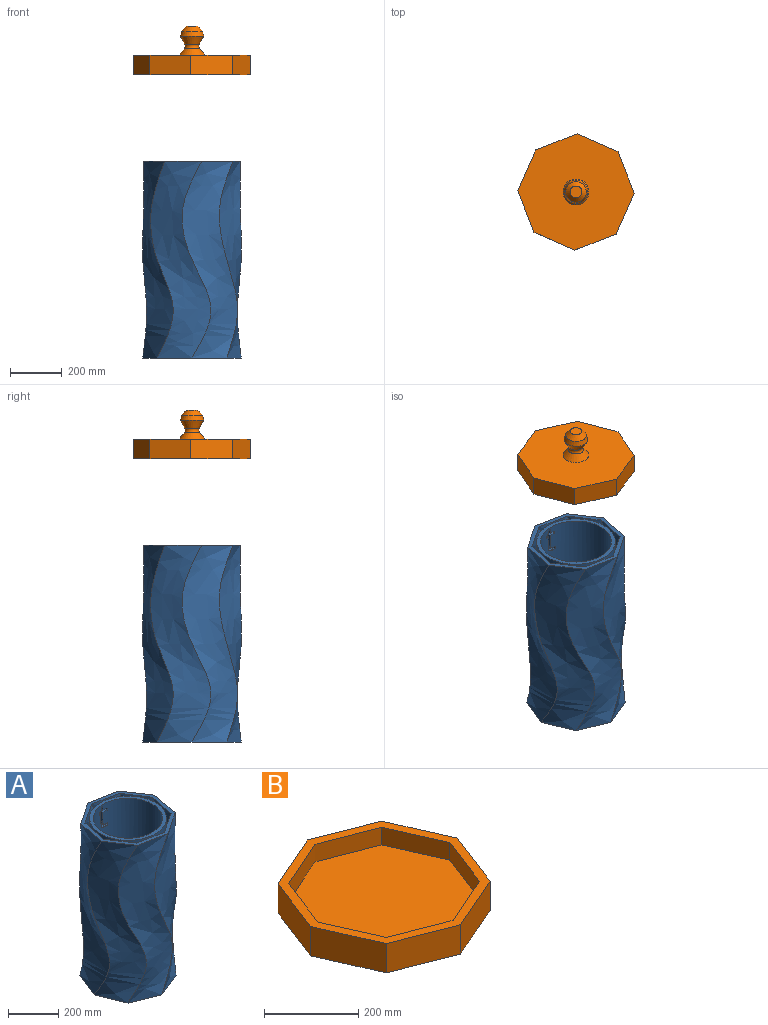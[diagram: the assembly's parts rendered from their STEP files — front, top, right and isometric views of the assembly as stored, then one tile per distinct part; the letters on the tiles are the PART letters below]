
ASSEMBLY  parts=2 mates=2
PART A: 212 faces, bbox 425.9x425.9x799.9 mm
  f0: plane 343.68x343.68mm, normal (0,0,1), area 70478.9mm2, adj f1,f3,f4,f6,f17,f18,f19,f20
  f1: cylinder r=137.18mm len=746.76mm, axis (0,0,-1), area 625380mm2, adj f0,f2,f27,f28,f29,f30,f31,f32
  f2: cylinder r=137.18mm len=34.63mm, axis (0,0,-1), area 741.5mm2, adj f1,f93,f94,f95,f96,f97,f98,f99
  f3: cylinder r=137.18mm len=48.52mm, axis (0,0,-1), area 1293.6mm2, adj f0,f128,f129,f130,f131,f132,f135
  f4: cylinder r=152.42mm len=746.76mm, axis (0,0,-1), area 696902.1mm2, adj f0,f5,f27,f28,f29,f30,f31,f32
  f5: cylinder r=152.42mm len=34.63mm, axis (0,0,-1), area 741mm2, adj f4,f93,f94,f95,f96,f97,f98,f99
  f6: cylinder r=152.42mm len=48.52mm, axis (0,0,-1), area 1293.2mm2, adj f0,f128,f129,f130,f131,f132,f135
  f7: plane 373.92x373.92mm, normal (0,0,1), area 17183mm2, adj f9,f10,f11,f12,f13,f14,f15,f16
  f8: plane 381x381mm, normal (0,0,-1), area 102644.3mm2, adj f9,f10,f11,f12,f13,f14,f15,f16
  f9: bspline ~769.42x258.19mm, area 110884.9mm2, adj f7,f8,f10,f16
  f10: bspline ~769.42x285.68mm, area 110884.9mm2, adj f7,f8,f9,f11
  f11: bspline ~769.42x258.19mm, area 110884.9mm2, adj f7,f8,f10,f12
  f12: bspline ~769.42x285.68mm, area 110884.9mm2, adj f7,f8,f11,f13
  f13: bspline ~769.42x258.19mm, area 110884.9mm2, adj f7,f8,f12,f14
  f14: bspline ~769.42x285.68mm, area 110884.9mm2, adj f7,f8,f13,f15
  f15: bspline ~769.42x258.19mm, area 110884.9mm2, adj f7,f8,f14,f16
  f16: bspline ~769.42x285.68mm, area 110884.9mm2, adj f7,f8,f9,f15
  f17: offset ~799.9x288.67mm, area 99034mm2, adj f0,f7,f18,f24
  f18: offset ~799.9x316.15mm, area 99034mm2, adj f0,f7,f17,f19
  f19: offset ~799.9x288.67mm, area 99034mm2, adj f0,f7,f18,f20
  f20: offset ~799.9x316.15mm, area 99034mm2, adj f0,f7,f19,f21
  f21: offset ~799.9x288.67mm, area 99034mm2, adj f0,f7,f20,f22
  f22: offset ~799.9x316.15mm, area 99034mm2, adj f0,f7,f21,f23
  f23: offset ~799.9x288.67mm, area 99034mm2, adj f0,f7,f22,f24
  f24: offset ~799.9x316.15mm, area 99034mm2, adj f0,f7,f17,f23
  f25: cylinder r=137.18mm len=48.52mm, axis (0,0,-1), area 1293.6mm2, adj f0,f104,f105,f106,f107,f108,f109
  f26: cylinder r=152.42mm len=48.52mm, axis (0,0,-1), area 1293.2mm2, adj f0,f104,f105,f106,f107,f108,f109
  f27: plane 304.84x304.84mm, normal (0,0,1), area 13865.6mm2, adj f1,f4
  f28: plane 15.64x9.99mm, normal (-0.99,0,0.15), area 155.6mm2, adj f1,f4,f29,f40
  f29: extruded ~16.26x7.78mm, area 120.7mm2, adj f1,f4,f28,f30
  f30: extruded ~15.84x14.76mm, area 257.8mm2, adj f1,f4,f29,f31
  f31: extruded ~17.45x15.46mm, area 288.5mm2, adj f1,f4,f30,f32
  f32: plane 38.15x15.26mm, normal (-1,0,0), area 582.3mm2, adj f1,f4,f31,f33
  f33: plane 16.32x10.77mm, normal (0,0,1), area 164.9mm2, adj f1,f4,f32,f34
  f34: plane 71.09x15.37mm, normal (1,0,0), area 1092.6mm2, adj f1,f4,f33,f35
  f35: plane 16.21x8.88mm, normal (0,0,-1), area 136.1mm2, adj f1,f4,f34,f36
  f36: plane 15.35x13.16mm, normal (-1,0,-0.09), area 201.9mm2, adj f1,f4,f35,f37
  f37: plane 15.3x0.52mm, normal (0,0,-1), area 7.9mm2, adj f1,f4,f36,f38
  f38: extruded ~15.47x10.7mm, area 220.5mm2, adj f1,f4,f37,f39
  f39: extruded ~15.92x12.27mm, area 199mm2, adj f1,f4,f38,f40
  f40: extruded ~16.43x8.49mm, area 131.2mm2, adj f1,f4,f28,f39
  f41: extruded ~16.43x8.49mm, area 131.2mm2, adj f1,f4,f42,f53
  f42: extruded ~15.92x12.27mm, area 199mm2, adj f1,f4,f41,f43
  f43: extruded ~15.47x10.7mm, area 220.5mm2, adj f1,f4,f42,f44
  f44: plane 15.3x0.52mm, normal (0,0,-1), area 7.9mm2, adj f1,f4,f43,f45
  f45: plane 15.35x13.16mm, normal (-1,0,-0.09), area 201.9mm2, adj f1,f4,f44,f46
  f46: plane 16.21x8.88mm, normal (0,0,-1), area 136.1mm2, adj f1,f4,f45,f47
  f47: plane 71.09x15.37mm, normal (1,0,0), area 1092.6mm2, adj f1,f4,f46,f48
  f48: plane 16.32x10.77mm, normal (0,0,1), area 164.9mm2, adj f1,f4,f47,f49
  f49: plane 38.15x15.26mm, normal (-1,0,0), area 582.3mm2, adj f1,f4,f48,f50
  f50: extruded ~17.45x15.46mm, area 288.5mm2, adj f1,f4,f49,f51
  f51: extruded ~15.84x14.76mm, area 257.8mm2, adj f1,f4,f50,f52
  f52: extruded ~16.26x7.78mm, area 120.7mm2, adj f1,f4,f51,f53
  f53: plane 15.64x9.99mm, normal (-0.99,0,0.15), area 155.6mm2, adj f1,f4,f41,f52
  f54: extruded ~19.21x16.14mm, area 308.3mm2, adj f1,f4,f55,f78
  f55: extruded ~20.4x17.26mm, area 322.7mm2, adj f1,f4,f54,f56
  f56: plane 15.45x9.24mm, normal (1,0,0), area 142.7mm2, adj f1,f4,f55,f57
  f57: extruded ~16.69x10.17mm, area 167.1mm2, adj f1,f4,f56,f58
  f58: extruded ~15.87x10.48mm, area 161.8mm2, adj f1,f4,f57,f59
  f59: extruded ~15.51x11.99mm, area 189mm2, adj f1,f4,f58,f60
  f60: extruded ~15.61x7.6mm, area 139.5mm2, adj f1,f4,f59,f61
  f61: extruded ~15.56x6.57mm, area 116.6mm2, adj f1,f4,f60,f62
  f62: extruded ~15.57x13mm, area 222.2mm2, adj f1,f4,f61,f63
  f63: extruded ~16.16x13.05mm, area 219.8mm2, adj f1,f4,f62,f64
  f64: extruded ~16.14x5.79mm, area 126.7mm2, adj f1,f4,f63,f65
  f65: extruded ~15.74x7.73mm, area 124.3mm2, adj f1,f4,f64,f66
  f66: extruded ~16.34x12.71mm, area 229.5mm2, adj f1,f4,f65,f67
  f67: extruded ~17.94x16.33mm, area 287.9mm2, adj f1,f4,f66,f68
  f68: extruded ~20.78x16.93mm, area 327.5mm2, adj f1,f4,f67,f69
  f69: plane 15.88x8.11mm, normal (-0.92,0,0.4), area 136.1mm2, adj f1,f4,f68,f70
  f70: extruded ~17.94x16.41mm, area 283.2mm2, adj f1,f4,f69,f71
  f71: extruded ~15.66x10.69mm, area 168.6mm2, adj f1,f4,f70,f72
  f72: extruded ~15.61x6.12mm, area 114mm2, adj f1,f4,f71,f73
  f73: extruded ~15.44x4.5mm, area 73.2mm2, adj f1,f4,f72,f74
  f74: extruded ~15.61x4.35mm, area 86.3mm2, adj f1,f4,f73,f75
  f75: extruded ~15.48x11.52mm, area 191mm2, adj f1,f4,f74,f76
  f76: extruded ~16.49x15.81mm, area 277.2mm2, adj f1,f4,f75,f77
  f77: extruded ~16x10.87mm, area 183.6mm2, adj f1,f4,f76,f78
  f78: extruded ~16.31x14.16mm, area 252mm2, adj f1,f4,f54,f77
  f79: extruded ~16.31x14.16mm, area 252mm2, adj f1,f4,f80,f103
  f80: extruded ~16x10.87mm, area 183.6mm2, adj f1,f4,f79,f81
  f81: extruded ~16.49x15.81mm, area 277.2mm2, adj f1,f4,f80,f82
  f82: extruded ~15.48x11.52mm, area 191mm2, adj f1,f4,f81,f83
  f83: extruded ~15.61x4.35mm, area 86.3mm2, adj f1,f4,f82,f84
  f84: extruded ~15.44x4.5mm, area 73.2mm2, adj f1,f4,f83,f85
  f85: extruded ~15.61x6.12mm, area 114mm2, adj f1,f4,f84,f86
  f86: extruded ~15.66x10.69mm, area 168.6mm2, adj f1,f4,f85,f87
  f87: extruded ~17.94x16.41mm, area 283.2mm2, adj f1,f4,f86,f88
  f88: plane 15.88x8.11mm, normal (-0.92,0,0.4), area 136.1mm2, adj f1,f4,f87,f89
  f89: extruded ~20.78x16.93mm, area 327.5mm2, adj f1,f4,f88,f90
  f90: extruded ~17.94x16.33mm, area 287.9mm2, adj f1,f4,f89,f91
  f91: extruded ~16.34x12.71mm, area 229.7mm2, adj f1,f4,f90,f92
  f92: extruded ~15.74x7.73mm, area 124.3mm2, adj f1,f4,f91,f93
  f93: extruded ~16.14x5.79mm, area 126.7mm2, adj f1,f2,f4,f5,f92,f94
  f94: extruded ~16.16x13.05mm, area 219.8mm2, adj f2,f5,f93,f95
  f95: extruded ~15.57x13mm, area 222.2mm2, adj f2,f5,f94,f96
  f96: extruded ~15.56x6.57mm, area 116.6mm2, adj f2,f5,f95,f97
  f97: extruded ~15.61x7.6mm, area 139.5mm2, adj f2,f5,f96,f98
  f98: extruded ~15.51x11.99mm, area 189mm2, adj f2,f5,f97,f99
  f99: extruded ~15.87x10.48mm, area 161.8mm2, adj f2,f5,f98,f100
  f100: extruded ~16.69x10.17mm, area 167.1mm2, adj f1,f2,f4,f5,f99,f101
  f101: plane 15.45x9.24mm, normal (1,0,0), area 142.7mm2, adj f1,f4,f100,f102
  f102: extruded ~20.4x17.26mm, area 322.6mm2, adj f1,f4,f101,f103
  f103: extruded ~19.21x16.14mm, area 308.3mm2, adj f1,f4,f79,f102
  f104: extruded ~15.62x9.95mm, area 163mm2, adj f25,f26,f105,f109
  f105: extruded ~15.81x9.52mm, area 158.3mm2, adj f25,f26,f104,f106
  f106: extruded ~15.51x12.56mm, area 211.3mm2, adj f25,f26,f105,f107
  f107: extruded ~15.59x15.32mm, area 246.6mm2, adj f25,f26,f106,f108
  f108: plane 28.52x15.3mm, normal (-1,0,0), area 436.5mm2, adj f0,f25,f26,f107
  f109: plane 35.29x15.33mm, normal (1,0,0), area 541.1mm2, adj f0,f25,f26,f104
  f110: plane 77.44x15.41mm, normal (1,0,0), area 1193.4mm2, adj f0,f1,f4,f111
  f111: plane 16.35x8.27mm, normal (0,0,-1), area 126.9mm2, adj f1,f4,f110,f112
  f112: plane 23.44x15.3mm, normal (-1,0,0), area 358.7mm2, adj f1,f4,f111,f113
  f113: extruded ~15.34x7.02mm, area 107.7mm2, adj f1,f4,f112,f114
  f114: plane 15.35x0.49mm, normal (0,0,-1), area 7.6mm2, adj f1,f4,f113,f115
  f115: extruded ~15.74x6.94mm, area 144mm2, adj f1,f4,f114,f116
  f116: extruded ~15.32x10.27mm, area 161.9mm2, adj f1,f4,f115,f117
  f117: extruded ~16.53x15.01mm, area 246.9mm2, adj f1,f4,f116,f118
  f118: extruded ~16.18x15.1mm, area 252.3mm2, adj f1,f4,f117,f119
  f119: plane 35.58x15.46mm, normal (-1,0,0), area 549.9mm2, adj f0,f1,f4,f118
  f120: extruded ~16.18x15.1mm, area 252.3mm2, adj f1,f4,f121,f133
  f121: extruded ~16.53x15.01mm, area 246.9mm2, adj f1,f4,f120,f122
  f122: extruded ~15.32x10.27mm, area 161.9mm2, adj f1,f4,f121,f123
  f123: extruded ~15.74x6.94mm, area 144mm2, adj f1,f4,f122,f124
  f124: plane 15.35x0.49mm, normal (0,0,-1), area 7.6mm2, adj f1,f4,f123,f125
  f125: extruded ~15.34x7.02mm, area 107.7mm2, adj f1,f4,f124,f126
  f126: plane 23.44x15.3mm, normal (-1,0,0), area 358.7mm2, adj f1,f4,f125,f127
  f127: plane 16.35x8.27mm, normal (0,0,-1), area 126.9mm2, adj f1,f4,f126,f134
  f128: extruded ~15.59x15.32mm, area 246.6mm2, adj f3,f6,f129,f135
  f129: extruded ~15.51x12.56mm, area 211.3mm2, adj f3,f6,f128,f130
  f130: extruded ~15.81x9.52mm, area 158.3mm2, adj f3,f6,f129,f131
  f131: extruded ~15.62x9.95mm, area 163mm2, adj f3,f6,f130,f132
  f132: plane 35.29x15.33mm, normal (1,0,0), area 541.1mm2, adj f0,f3,f6,f131
  f133: plane 35.58x15.46mm, normal (-1,0,0), area 549.9mm2, adj f0,f1,f4,f120
  f134: plane 77.44x15.41mm, normal (1,0,0), area 1193.4mm2, adj f0,f1,f4,f127
  f135: plane 28.52x15.3mm, normal (-1,0,0), area 436.5mm2, adj f0,f3,f6,f128
  f136: plane 15.36x0.44mm, normal (0,0,1), area 6.8mm2, adj f1,f4,f137,f154
  f137: extruded ~15.9x9mm, area 182.8mm2, adj f1,f4,f136,f138
  f138: extruded ~15.27x11.23mm, area 175.3mm2, adj f1,f4,f137,f139
  f139: extruded ~16.58x14.08mm, area 232.4mm2, adj f1,f4,f138,f140
  f140: extruded ~16.23x13.18mm, area 224.8mm2, adj f1,f4,f139,f141
  f141: extruded ~29.26x19.17mm, area 602.9mm2, adj f1,f4,f140,f142
  f142: plane 15.95x10.25mm, normal (0.03,0,-1), area 156.6mm2, adj f1,f4,f141,f143
  f143: plane 15.32x3.76mm, normal (1,0,0), area 57.5mm2, adj f1,f4,f142,f144
  f144: extruded ~15.58x10.5mm, area 171mm2, adj f1,f4,f143,f145
  f145: extruded ~15.71x9.79mm, area 162.9mm2, adj f1,f4,f144,f146
  f146: extruded ~17.07x16.1mm, area 272.7mm2, adj f1,f4,f145,f147
  f147: plane 15.68x7.01mm, normal (0.93,0,0.37), area 115.8mm2, adj f1,f4,f146,f148
  f148: extruded ~16.22x9.78mm, area 161mm2, adj f1,f4,f147,f149
  f149: extruded ~15.48x10.68mm, area 164.7mm2, adj f1,f4,f148,f150
  f150: extruded ~16.44x16.01mm, area 261.5mm2, adj f1,f4,f149,f151
  f151: extruded ~16.17x15.37mm, area 257.4mm2, adj f1,f4,f150,f152
  f152: plane 41.24x15.44mm, normal (-1,0,0), area 636.9mm2, adj f1,f4,f151,f153
  f153: plane 16.35x6.79mm, normal (0,0,1), area 104.5mm2, adj f1,f4,f152,f154
  f154: plane 15.53x8.61mm, normal (0.98,0,0.21), area 134.9mm2, adj f1,f4,f136,f153
  f155: plane 15.53x8.61mm, normal (0.98,0,0.21), area 134.9mm2, adj f1,f4,f156,f173
  f156: plane 16.35x6.79mm, normal (0,0,1), area 104.5mm2, adj f1,f4,f155,f157
  f157: plane 41.24x15.44mm, normal (-1,0,0), area 636.9mm2, adj f1,f4,f156,f158
  f158: extruded ~16.17x15.37mm, area 257.4mm2, adj f1,f4,f157,f159
  f159: extruded ~16.44x16.01mm, area 261.5mm2, adj f1,f4,f158,f160
  f160: extruded ~15.48x10.68mm, area 164.7mm2, adj f1,f4,f159,f161
  f161: extruded ~16.22x9.78mm, area 161mm2, adj f1,f4,f160,f162
  f162: plane 15.68x7.01mm, normal (0.93,0,0.37), area 115.8mm2, adj f1,f4,f161,f163
  f163: extruded ~17.07x16.1mm, area 272.7mm2, adj f1,f4,f162,f164
  f164: extruded ~15.71x9.79mm, area 162.9mm2, adj f1,f4,f163,f165
  f165: extruded ~15.58x10.5mm, area 171mm2, adj f1,f4,f164,f166
  f166: plane 15.32x3.76mm, normal (1,0,0), area 57.5mm2, adj f1,f4,f165,f167
  f167: plane 15.95x10.25mm, normal (0.03,0,-1), area 156.6mm2, adj f1,f4,f166,f168
  f168: extruded ~29.26x19.17mm, area 602.8mm2, adj f1,f4,f167,f169
  f169: extruded ~16.23x13.18mm, area 224.9mm2, adj f1,f4,f168,f170
  f170: extruded ~16.58x14.08mm, area 232.4mm2, adj f1,f4,f169,f171
  f171: extruded ~15.27x11.23mm, area 175.3mm2, adj f1,f4,f170,f172
  f172: extruded ~15.9x9mm, area 182.8mm2, adj f1,f4,f171,f173
  f173: plane 15.36x0.44mm, normal (0,0,1), area 6.8mm2, adj f1,f4,f155,f172
  f174: extruded ~15.99x4.87mm, area 76.5mm2, adj f1,f4,f175,f192
  f175: plane 15.4x9.53mm, normal (-1,0,0), area 146.7mm2, adj f1,f4,f174,f176
  f176: extruded ~16.1x5.95mm, area 95mm2, adj f1,f4,f175,f177
  f177: extruded ~15.85x7.1mm, area 109.2mm2, adj f1,f4,f176,f178
  f178: extruded ~25.13x23.83mm, area 608mm2, adj f1,f4,f177,f179
  f179: plane 48.91x15.34mm, normal (1,0,0), area 750.1mm2, adj f1,f4,f178,f180
  f180: plane 17.25x11.78mm, normal (0,0,1), area 181.7mm2, adj f1,f4,f179,f181
  f181: plane 15.53x6mm, normal (1,0,0), area 93.2mm2, adj f1,f4,f180,f182
  f182: plane 17.27x11.8mm, normal (0.4,0,-0.92), area 198.6mm2, adj f1,f4,f181,f183
  f183: plane 17.56x15.81mm, normal (0.96,0,-0.29), area 280.2mm2, adj f1,f4,f182,f184
  f184: plane 15.62x7.2mm, normal (0,0,-1), area 109.9mm2, adj f1,f4,f183,f185
  f185: plane 19.06x15.24mm, normal (-1,0,0), area 290.5mm2, adj f1,f4,f184,f186
  f186: plane 23.86x16.74mm, normal (0,0,-1), area 364.6mm2, adj f1,f4,f185,f187
  f187: plane 15.39x9.67mm, normal (-1,0,0), area 148.9mm2, adj f1,f4,f186,f188
  f188: plane 23.86x16.74mm, normal (0,0,1), area 364.6mm2, adj f1,f4,f187,f189
  f189: plane 48.38x15.24mm, normal (-1,0,0), area 737.6mm2, adj f1,f4,f188,f190
  f190: extruded ~15.29x11.39mm, area 185.8mm2, adj f1,f4,f189,f191
  f191: extruded ~15.57x9.67mm, area 164.7mm2, adj f1,f4,f190,f192
  f192: extruded ~15.87x6.38mm, area 98.1mm2, adj f1,f4,f174,f191
  f193: extruded ~15.87x6.38mm, area 98.1mm2, adj f1,f4,f194,f211
  f194: extruded ~15.57x9.67mm, area 164.7mm2, adj f1,f4,f193,f195
  f195: extruded ~15.29x11.39mm, area 185.8mm2, adj f1,f4,f194,f196
  f196: plane 48.38x15.24mm, normal (-1,0,0), area 737.6mm2, adj f1,f4,f195,f197
  f197: plane 23.86x16.74mm, normal (0,0,1), area 364.6mm2, adj f1,f4,f196,f198
  f198: plane 15.39x9.67mm, normal (-1,0,0), area 148.9mm2, adj f1,f4,f197,f199
  f199: plane 23.86x16.74mm, normal (0,0,-1), area 364.6mm2, adj f1,f4,f198,f200
  f200: plane 19.06x15.24mm, normal (-1,0,0), area 290.5mm2, adj f1,f4,f199,f201
  f201: plane 15.62x7.2mm, normal (0,0,-1), area 109.9mm2, adj f1,f4,f200,f202
  f202: plane 17.56x15.81mm, normal (0.96,0,-0.29), area 280.2mm2, adj f1,f4,f201,f203
  f203: plane 17.25x11.79mm, normal (0.4,0,-0.92), area 198.6mm2, adj f1,f4,f202,f204
  f204: plane 15.53x6mm, normal (1,0,0), area 93.2mm2, adj f1,f4,f203,f205
  f205: plane 17.25x11.78mm, normal (0,0,1), area 181.7mm2, adj f1,f4,f204,f206
  f206: plane 48.91x15.34mm, normal (1,0,0), area 750.1mm2, adj f1,f4,f205,f207
  f207: extruded ~25.13x23.83mm, area 608mm2, adj f1,f4,f206,f208
  f208: extruded ~15.85x7.1mm, area 109.2mm2, adj f1,f4,f207,f209
  f209: extruded ~16.1x5.95mm, area 95mm2, adj f1,f4,f208,f210
  f210: plane 15.4x9.53mm, normal (-1,0,0), area 146.7mm2, adj f1,f4,f209,f211
  f211: extruded ~15.99x4.87mm, area 76.5mm2, adj f1,f4,f193,f210
PART B: 25 faces, bbox 450.7x450.7x188.9 mm
  f0: plane 157.97x76.2mm, normal (-0.4,0.92,0), area 13144.9mm2, adj f1,f15,f16,f17
  f1: plane 160.71x76.2mm, normal (-0.93,0.36,0), area 13144.9mm2, adj f0,f2,f16,f17
  f2: plane 157.97x76.2mm, normal (-0.92,-0.4,0), area 13144.9mm2, adj f1,f3,f16,f17
  f3: plane 160.71x76.2mm, normal (-0.36,-0.93,0), area 13144.9mm2, adj f2,f4,f16,f17
  f4: plane 157.97x76.2mm, normal (0.4,-0.92,0), area 13144.9mm2, adj f3,f5,f16,f17
  f5: plane 160.71x76.2mm, normal (0.93,-0.36,0), area 13144.9mm2, adj f4,f6,f16,f17
  f6: plane 157.97x76.2mm, normal (0.92,0.4,0), area 13144.9mm2, adj f5,f15,f16,f17
  f7: plane 142.05x62.71mm, normal (0.4,-0.91,0), area 7099.3mm2, adj f8,f14,f16,f18
  f8: plane 144.79x56.11mm, normal (-0.36,-0.93,0), area 7099.3mm2, adj f7,f9,f16,f18
  f9: plane 142.05x62.71mm, normal (-0.91,-0.4,0), area 7099.3mm2, adj f8,f10,f16,f18
  f10: plane 144.79x56.11mm, normal (-0.93,0.36,0), area 7099.3mm2, adj f9,f11,f16,f18
  f11: plane 142.05x62.71mm, normal (-0.4,0.91,0), area 7099.3mm2, adj f10,f12,f16,f18
  f12: plane 144.79x56.11mm, normal (0.36,0.93,0), area 7099.3mm2, adj f11,f13,f16,f18
  f13: plane 142.05x62.71mm, normal (0.91,0.4,0), area 7099.3mm2, adj f12,f14,f16,f18
  f14: plane 144.79x56.11mm, normal (0.93,-0.36,0), area 7099.3mm2, adj f7,f13,f16,f18
  f15: plane 160.71x76.2mm, normal (0.36,0.93,0), area 13144.9mm2, adj f0,f6,f16,f17
  f16: plane 450.68x450.68mm, normal (0,0,1), area 27266.7mm2, adj f0,f1,f2,f3,f4,f5,f6,f7
  f17: plane 450.68x450.68mm, normal (0,0,-1), area 135739mm2, adj f0,f1,f2,f3,f4,f5,f6,f15
  f18: plane 405.65x405.65mm, normal (0,0,1), area 116418.3mm2, adj f7,f8,f9,f10,f11,f12,f13,f14
  f19: cone r=40mm half-angle=40.9deg, axis (0,0,1), area 5172.3mm2, adj f20,f24
  f20: plane 45.72x45.72mm, normal (0,0,-1), area 1641.7mm2, adj f19
  f21: cone r=29.53mm half-angle=39.3deg, axis (0,0,1), area 8222.4mm2, adj f17,f22
  f22: torus R=41.32mm, axis (0,0,1), area 3131.5mm2, adj f21,f23
  f23: cone r=28.13mm half-angle=30deg, axis (0,0,-1), area 8163.6mm2, adj f22,f24
  f24: cone r=45.72mm half-angle=16.1deg, axis (0,0,1), area 5549.4mm2, adj f19,f23
PLACE A t=(-52.75,72.81,-197.85)mm fixed
PLACE B rot(axis=(0,1,0),180deg) t=(-52.75,72.81,974.88)mm
MATE slider A.f1 <-> B.f22  axis (0,0,-1) through (-52.75,72.81,190.77)mm
MATE parallel B.f22 <-> A.f1  axis (0,0,-1) through (-52.75,72.81,944.4)mm
